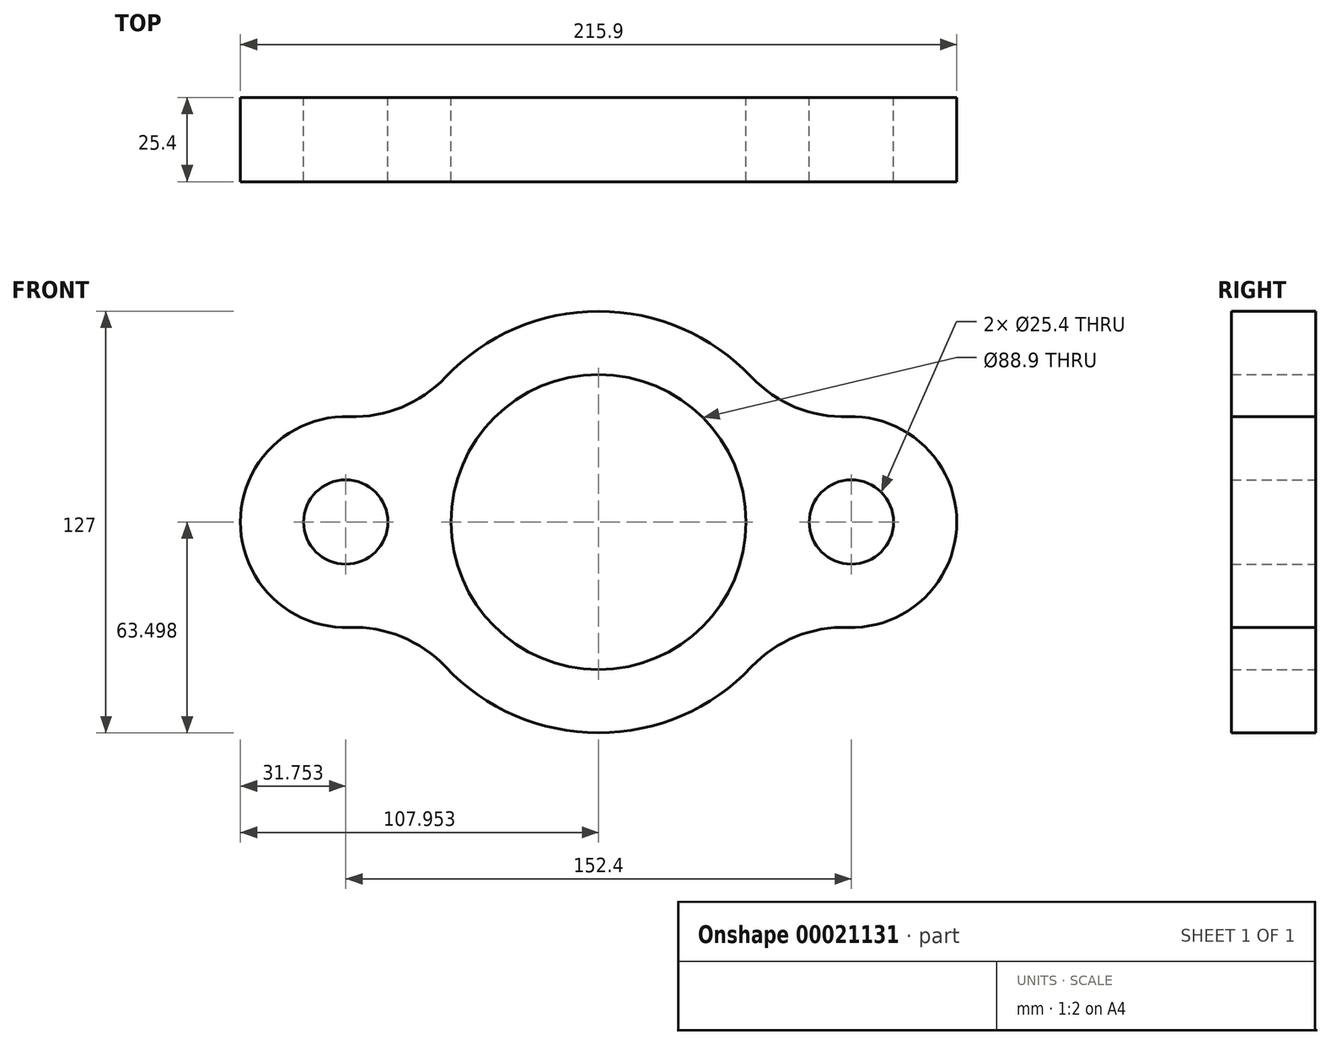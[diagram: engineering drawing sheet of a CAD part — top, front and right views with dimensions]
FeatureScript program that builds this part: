
annotation { "Feature Type Name" : "Feature", "Feature Type Description" : "" }
export const myFeature = defineFeature(function(context is Context, id is Id, definition is map)
    precondition{}
    {
        {
            var Q0;
            Q0=qCreatedBy(makeId("Front.planeOp"),FACE);
            var sketch = newSketch(context, id + "F0", { "sketchPlane" : qUnion([Q0])});
            skCircle(sketch, "E0", {"center": v(-24.13, 9.4) * mm, "radius": 44.45 * mm});
            skCircle(sketch, "E1", {"center": v(-100.33, 9.4) * mm, "radius": 12.7 * mm});
            skCircle(sketch, "E2", {"center": v(52.07, 9.4) * mm, "radius": 12.7 * mm});
            skCircle(sketch, "E3", {"center": v(52.07, 9.4) * mm, "radius": 31.75 * mm});
            skCircle(sketch, "E4", {"center": v(-100.33, 9.4) * mm, "radius": 31.75 * mm});
            skCircle(sketch, "E5", {"center": v(-24.13, 9.4) * mm, "radius": 63.5 * mm});
            skArc(sketch, "E6", {"start": v(-99.24, 41.13) * mm, "mid": v(-83.47, 43.96) * mm, "end": v(-70.26, 53.03) * mm});
            skArc(sketch, "E7", {"start": v(-70.26, -34.23) * mm, "mid": v(-83.47, -25.17) * mm, "end": v(-99.24, -22.33) * mm});
            skArc(sketch, "E8", {"start": v(51, -22.33) * mm, "mid": v(35.22, -25.17) * mm, "end": v(22, -34.23) * mm});
            skArc(sketch, "E9", {"start": v(22, 53.03) * mm, "mid": v(35.22, 43.96) * mm, "end": v(51, 41.13) * mm});
            skSolve(sketch);
        }
        {
            var Q0;
            Q0 = qSketchRegion(id + "F0", true);
            var Q1;
            {var subQ1=sQuery(id+"F0.wireOp",EDGE,"E4");var subQ5=makeQuery(id+"F0.imprint","INTERSECT",VERTEX,{"derivedFrom":[sQuery(id+"F0.wireOp",EDGE,"E0"),subQ1]});Q1=makeQuery(id+"F0.imprint","IMPRINT",FACE,{"disambiguationData":[TD([[makeQuery(id+"F0.imprint","IMPRINT",EDGE,{"disambiguationData":[TD([[subQ5,-1.0]])],"derivedFrom":subQ1}),1.0]])]});}
            var Q2;
            {var subQ1=sQuery(id+"F0.wireOp",EDGE,"E3");var subQ5=makeQuery(id+"F0.imprint","INTERSECT",VERTEX,{"derivedFrom":[sQuery(id+"F0.wireOp",EDGE,"E0"),subQ1]});Q2=makeQuery(id+"F0.imprint","IMPRINT",FACE,{"disambiguationData":[TD([[makeQuery(id+"F0.imprint","IMPRINT",EDGE,{"disambiguationData":[TD([[subQ5,1.0]])],"derivedFrom":subQ1}),1.0]])]});}
            extrude(context, id + "F1", {"entities" : qUnion([Q0, Q1, Q2]), "depth" : 25.4 * mm});
        }
    });
